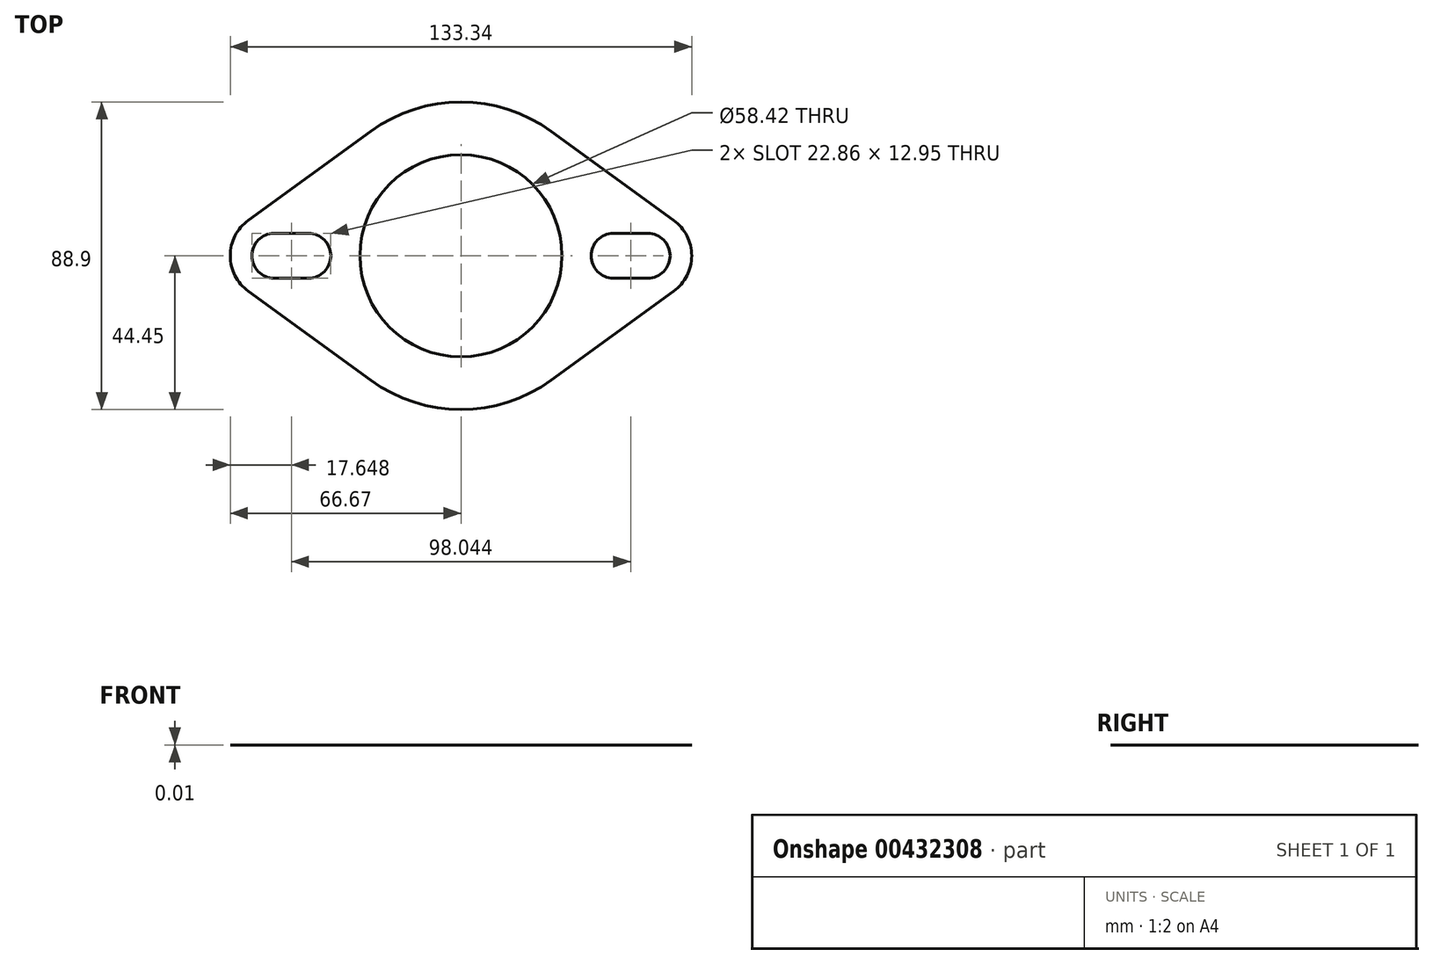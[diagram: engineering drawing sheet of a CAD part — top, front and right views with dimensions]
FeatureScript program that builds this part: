
annotation { "Feature Type Name" : "Feature", "Feature Type Description" : "" }
export const myFeature = defineFeature(function(context is Context, id is Id, definition is map)
    precondition{}
    {
        {
            var Q0;
            Q0=qCreatedBy(makeId("Top.planeOp"),FACE);
            var sketch = newSketch(context, id + "F0", { "sketchPlane" : qUnion([Q0])});
            skCircle(sketch, "E0", {"center": v(0, 0) * mm, "radius": 29.21 * mm});
            skArc(sketch, "E1", {"start": v(-44.07, -6.48) * mm, "mid": v(-37.6, 0) * mm, "end": v(-44.07, 6.48) * mm});
            skArc(sketch, "E2", {"start": v(-53.98, 6.48) * mm, "mid": v(-60.45, 0) * mm, "end": v(-53.98, -6.48) * mm});
            skArc(sketch, "E3", {"start": v(44.07, 6.48) * mm, "mid": v(37.6, 0) * mm, "end": v(44.07, -6.48) * mm});
            skArc(sketch, "E4", {"start": v(53.98, -6.48) * mm, "mid": v(60.45, 0) * mm, "end": v(53.97, 6.48) * mm});
            skArc(sketch, "E5", {"start": v(-26.15, -35.95) * mm, "mid": v(0, -44.45) * mm, "end": v(26.15, -35.95) * mm});
            skArc(sketch, "E6", {"start": v(-61.45, 10.27) * mm, "mid": v(-66.68, 0) * mm, "end": v(-61.45, -10.27) * mm});
            skArc(sketch, "E7", {"start": v(61.45, -10.27) * mm, "mid": v(66.68, 0) * mm, "end": v(61.45, 10.27) * mm});
            skLineSegment(sketch, "E8", {"start": v(-61.45, 10.27) * mm, "end": v(-26.15, 35.95) * mm});
            skLineSegment(sketch, "E9", {"start": v(-61.45, -10.27) * mm, "end": v(-26.15, -35.95) * mm});
            skLineSegment(sketch, "E10", {"start": v(26.15, -35.95) * mm, "end": v(61.45, -10.27) * mm});
            skLineSegment(sketch, "E11", {"start": v(61.45, 10.27) * mm, "end": v(26.15, 35.95) * mm});
            skArc(sketch, "E12.trimOffspring", {"start": v(26.15, 35.95) * mm, "mid": v(0, 44.45) * mm, "end": v(-26.15, 35.95) * mm});
            skLineSegment(sketch, "E13", {"start": v(-53.98, 6.48) * mm, "end": v(-44.07, 6.48) * mm});
            skLineSegment(sketch, "E14", {"start": v(-53.98, -6.48) * mm, "end": v(-44.07, -6.48) * mm});
            skLineSegment(sketch, "E15", {"start": v(44.07, 6.48) * mm, "end": v(53.97, 6.48) * mm});
            skLineSegment(sketch, "E16", {"start": v(53.98, -6.48) * mm, "end": v(44.07, -6.48) * mm});
            skPoint(sketch, "E17", {"position": v(-66.68, 0) * mm});
            skPoint(sketch, "E18", {"position": v(66.68, 0) * mm});
            skPoint(sketch, "E19", {"position": v(-60.45, 0) * mm});
            skPoint(sketch, "E20", {"position": v(-37.6, 0) * mm});
            skPoint(sketch, "E21", {"position": v(37.6, 0) * mm});
            skPoint(sketch, "E22", {"position": v(60.45, 0) * mm});
            skLineSegment(sketch, "E23", {"start": v(-37.6, 0) * mm, "end": v(37.6, 0) * mm, "construction": true});
            skSolve(sketch);
        }
        {
            var Q0;
            Q0=makeQuery(id+"F0.imprint","IMPRINT",FACE,{"disambiguationData":[TD([[makeQuery(id+"F0.imprint","IMPRINT",EDGE,{"derivedFrom":sQuery(id+"F0.wireOp",EDGE,"E0")}),-1.0]])]});
            extrude(context, id + "F1", {"entities" : qUnion([Q0]), "depth" : 5 / 406.4 * mm});
        }
    });
